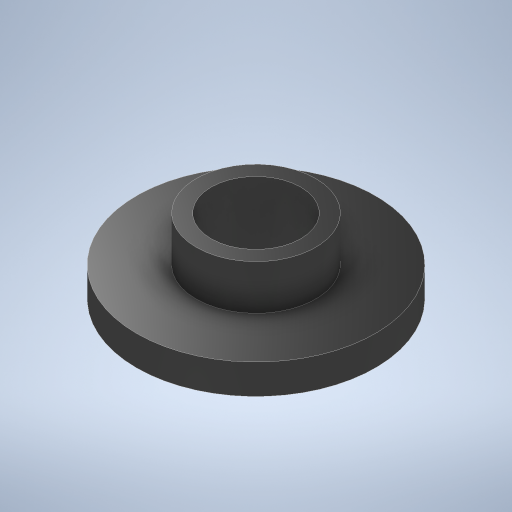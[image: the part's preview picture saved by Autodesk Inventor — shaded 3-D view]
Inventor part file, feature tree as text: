
AUTODESK INVENTOR PART (.ipt)
format: ipt  version: 2024.2 (Build 282272000, 272)  size: 252,928 bytes
history: native  units: mm
features: revolve x1, sketch x1
ambient origin geometry x8: Origin, YZ Plane, XZ Plane, XY Plane, X Axis, Y Axis, Z Axis, Center Point
bodies: Solid1 (feature_tree)
feature tree (2):
  revolve  "Revolution1"  [1 undecoded]
  sketch  "Sketch1"  dims[d0=3.0mm d1=4.0mm d2=8.0mm d3=1.0mm d4=1.5mm d5=90.0deg]
note: 1 required parameter value undecoded (feature->parameter linkage not recoverable at this tier; creation-order binding heuristic only, values carry confidence <= 0.55)
